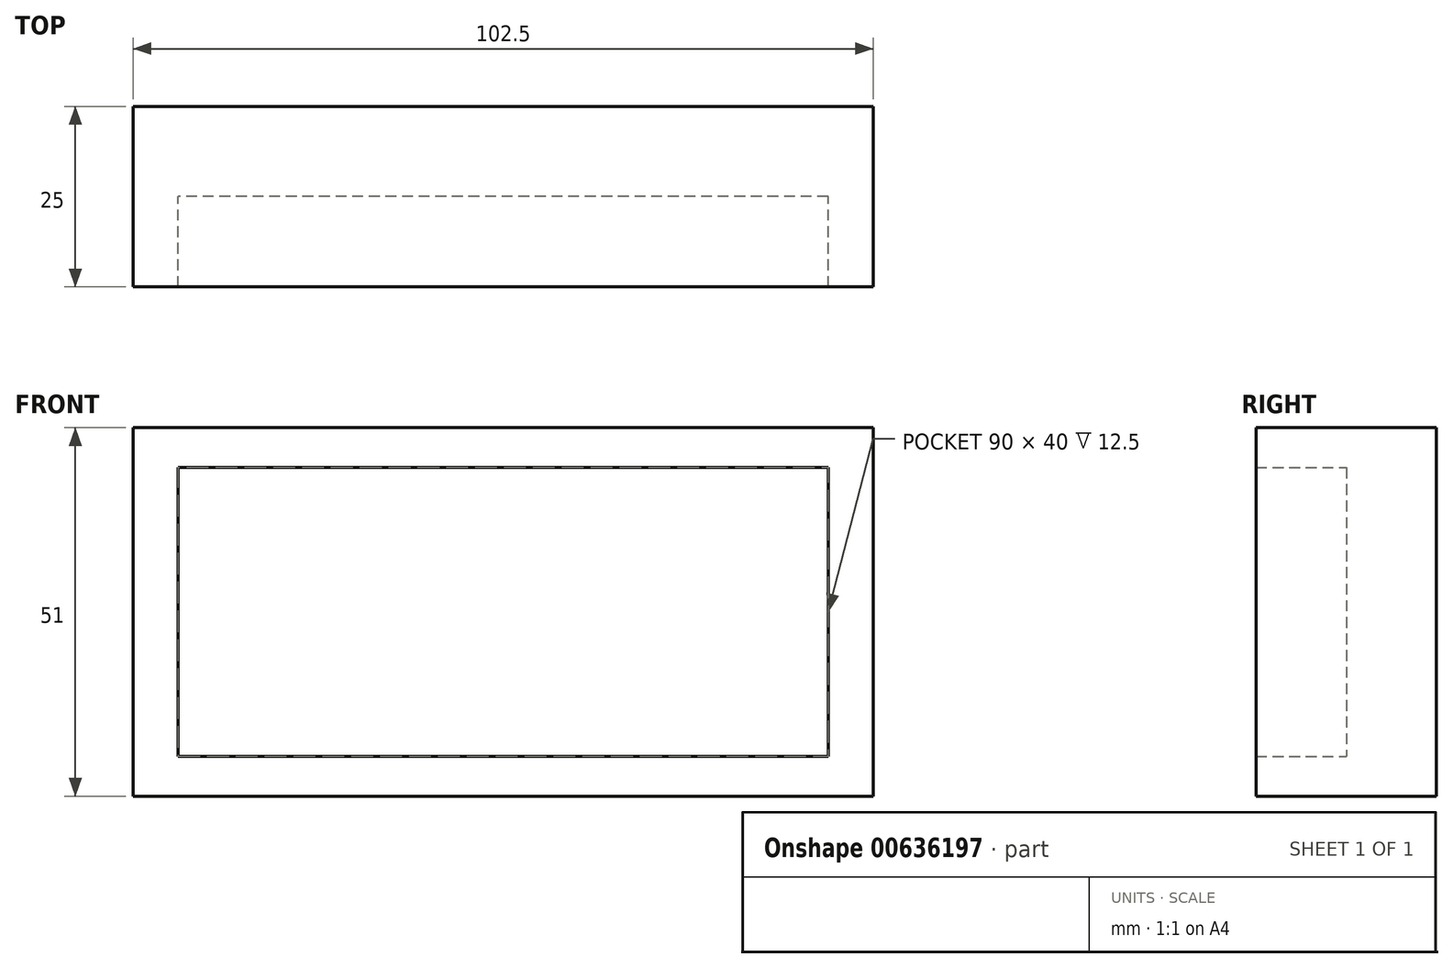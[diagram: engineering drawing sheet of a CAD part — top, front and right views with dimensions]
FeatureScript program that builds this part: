
annotation { "Feature Type Name" : "Feature", "Feature Type Description" : "" }
export const myFeature = defineFeature(function(context is Context, id is Id, definition is map)
    precondition{}
    {
        {
            var Q0;
            Q0=qCreatedBy(makeId("Front.planeOp"),FACE);
            var sketch = newSketch(context, id + "F0", { "sketchPlane" : qUnion([Q0])});
            skLineSegment(sketch, "E0.bottom", {"start": v(-51.25, 25.5) * mm, "end": v(51.25, 25.5) * mm});
            skLineSegment(sketch, "E0.top", {"start": v(-51.25, -25.5) * mm, "end": v(51.25, -25.5) * mm});
            skLineSegment(sketch, "E0.left", {"start": v(-51.25, 25.5) * mm, "end": v(-51.25, -25.5) * mm});
            skLineSegment(sketch, "E0.right", {"start": v(51.25, 25.5) * mm, "end": v(51.25, -25.5) * mm});
            skPoint(sketch, "E0.middle", {"position": v(0, 0) * mm});
            skSolve(sketch);
        }
        {
            var Q0;
            Q0=makeQuery(id+"F0.imprint","IMPRINT",FACE,{"disambiguationData":[TD([[makeQuery(id+"F0.imprint","IMPRINT",EDGE,{"derivedFrom":sQuery(id+"F0.wireOp",EDGE,"E0.bottom")}),-1.0]])]});
            extrude(context, id + "F1", {"entities" : qUnion([Q0]), "depth" : 25 * mm, "offsetDistance" : 25.4 * mm});
        }
        {
            var Q0;
            Q0=makeQuery(id+"F1.opExtrude","CAP_FACE",FACE,{"disambiguationData":[OSD([sQuery(id+"F0.wireOp",EDGE,"E0.bottom"),sQuery(id+"F0.wireOp",EDGE,"E0.top"),sQuery(id+"F0.wireOp",EDGE,"E0.left"),sQuery(id+"F0.wireOp",EDGE,"E0.right")])],"isStart":false});
            var sketch = newSketch(context, id + "F2", { "sketchPlane" : qUnion([Q0])});
            skLineSegment(sketch, "E1.bottom", {"start": v(45, 20) * mm, "end": v(-45, 20) * mm});
            skLineSegment(sketch, "E1.top", {"start": v(45, -20) * mm, "end": v(-45, -20) * mm});
            skLineSegment(sketch, "E1.left", {"start": v(45, 20) * mm, "end": v(45, -20) * mm});
            skLineSegment(sketch, "E1.right", {"start": v(-45, 20) * mm, "end": v(-45, -20) * mm});
            skPoint(sketch, "E1.middle", {"position": v(0, 0) * mm});
            skSolve(sketch);
        }
        {
            var Q0;
            Q0=makeQuery(id+"F2.imprint","IMPRINT",FACE,{"disambiguationData":[TD([[makeQuery(id+"F2.imprint","IMPRINT",EDGE,{"derivedFrom":sQuery(id+"F2.wireOp",EDGE,"E1.bottom")}),1.0]])]});
            extrude(context, id + "F3", {"entities" : qUnion([Q0]), "operationType" : NewBodyOperationType.REMOVE, "endBound" : BoundingType.SYMMETRIC, "depth" : 25 * mm, "offsetDistance" : 25 * mm});
        }
        {
            var Q0;
            Q0=makeQuery(id+"F2.imprint","IMPRINT",FACE,{"disambiguationData":[TD([[makeQuery(id+"F2.imprint","IMPRINT",EDGE,{"derivedFrom":sQuery(id+"F2.wireOp",EDGE,"E1.bottom")}),1.0]])]});
            var sketch = newSketch(context, id + "F4", { "sketchPlane" : qUnion([Q0])});
            skLineSegment(sketch, "E2.bottom", {"start": v(-32.61, -16.11) * mm, "end": v(-42.61, -16.11) * mm});
            skLineSegment(sketch, "E2.top", {"start": v(-32.61, -13.11) * mm, "end": v(-42.61, -13.11) * mm});
            skLineSegment(sketch, "E2.left", {"start": v(-32.61, -16.11) * mm, "end": v(-32.61, -13.11) * mm});
            skLineSegment(sketch, "E2.right", {"start": v(-42.61, -16.11) * mm, "end": v(-42.61, -13.11) * mm});
            skPoint(sketch, "E2.middle", {"position": v(-37.61, -14.61) * mm});
            skSolve(sketch);
        }
        {
            var Q0;
            Q0=makeQuery(id+"F2.imprint","IMPRINT",FACE,{"disambiguationData":[TD([[makeQuery(id+"F2.imprint","IMPRINT",EDGE,{"derivedFrom":sQuery(id+"F2.wireOp",EDGE,"E1.bottom")}),1.0]])]});
            var Q1;
            Q1=sQuery(id+"F4.wireOp",EDGE,"E2.top");
            var Q2;
            Q2=sQuery(id+"F4.wireOp",EDGE,"E2.right");
            var Q3;
            Q3=sQuery(id+"F4.wireOp",EDGE,"E2.left");
            var Q4;
            Q4=sQuery(id+"F4.wireOp",EDGE,"E2.bottom");
            extrude(context, id + "F5", {"entities" : qUnion([Q0]), "bodyType" : ToolBodyType.SURFACE, "surfaceEntities" : qUnion([Q1, Q2, Q3, Q4]), "depth" : 5 * mm, "offsetDistance" : 25 * mm});
        }
    });
